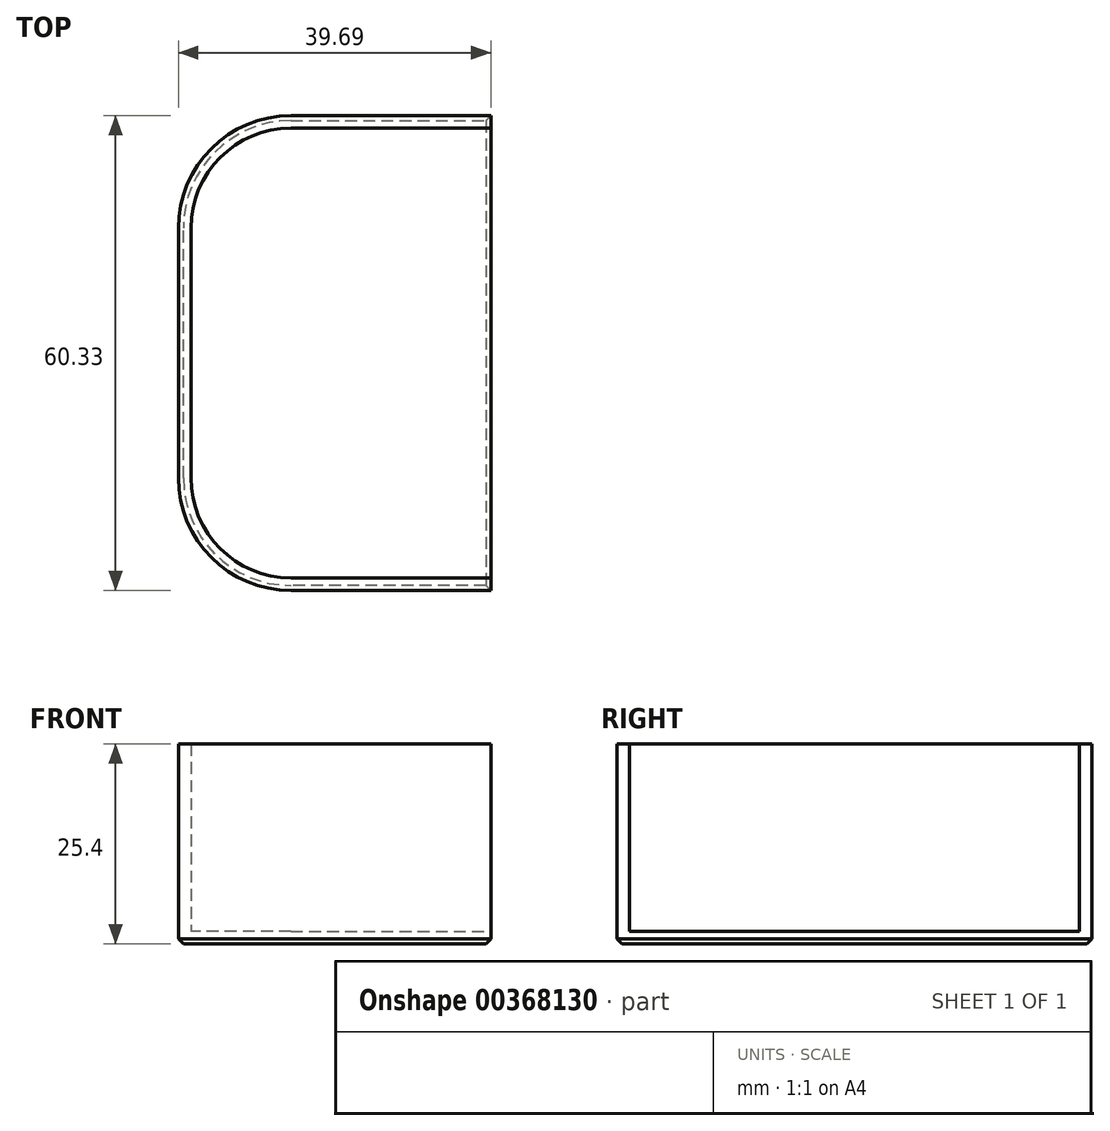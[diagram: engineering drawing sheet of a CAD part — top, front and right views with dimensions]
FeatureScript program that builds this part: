
annotation { "Feature Type Name" : "Feature", "Feature Type Description" : "" }
export const myFeature = defineFeature(function(context is Context, id is Id, definition is map)
    precondition{}
    {
        {
            var Q0;
            Q0=qCreatedBy(makeId("Top.planeOp"),FACE);
            var sketch = newSketch(context, id + "F0", { "sketchPlane" : qUnion([Q0])});
            skLineSegment(sketch, "E0.bottom", {"start": v(12.7, 0) * mm, "end": v(38.1, 0) * mm});
            skLineSegment(sketch, "E0.top", {"start": v(12.7, 57.15) * mm, "end": v(38.1, 57.15) * mm});
            skLineSegment(sketch, "E0.left", {"start": v(0, 12.7) * mm, "end": v(0, 44.45) * mm});
            skPoint(sketch, "E1.visualSharp", {"position": v(0, 57.15) * mm});
            skArc(sketch, "E1.filletArc", {"start": v(12.7, 57.15) * mm, "mid": v(3.72, 53.43) * mm, "end": v(0, 44.45) * mm});
            skPoint(sketch, "E2.visualSharp", {"position": v(0, 0) * mm});
            skArc(sketch, "E2.filletArc", {"start": v(0, 12.7) * mm, "mid": v(3.72, 3.72) * mm, "end": v(12.7, 0) * mm});
            skLineSegment(sketch, "E3", {"start": v(38.1, 57.15) * mm, "end": v(38.1, 58.74) * mm});
            skLineSegment(sketch, "E4", {"start": v(38.1, 58.74) * mm, "end": v(12.7, 58.74) * mm});
            skLineSegment(sketch, "E5", {"start": v(38.1, 0) * mm, "end": v(38.1, -1.59) * mm});
            skLineSegment(sketch, "E6", {"start": v(38.1, -1.59) * mm, "end": v(12.7, -1.59) * mm});
            skLineSegment(sketch, "E7", {"start": v(-1.59, 44.45) * mm, "end": v(-1.59, 12.7) * mm});
            skArc(sketch, "E8", {"start": v(12.7, 58.74) * mm, "mid": v(2.6, 54.55) * mm, "end": v(-1.59, 44.45) * mm});
            skArc(sketch, "E9", {"start": v(-1.59, 12.7) * mm, "mid": v(2.6, 2.6) * mm, "end": v(12.7, -1.59) * mm});
            skSolve(sketch);
        }
        {
            var Q0;
            Q0 = qSketchRegion(id + "F0", true);
            extrude(context, id + "F1", {"entities" : qUnion([Q0]), "depth" : 25.4 * mm});
        }
        {
            var Q0;
            Q0=makeQuery(id+"F1.opExtrude","CAP_FACE",FACE,{"disambiguationData":[OSD([sQuery(id+"F0.wireOp",EDGE,"E0.bottom"),sQuery(id+"F0.wireOp",EDGE,"E0.top"),sQuery(id+"F0.wireOp",EDGE,"E0.left"),sQuery(id+"F0.wireOp",EDGE,"E1.filletArc"),sQuery(id+"F0.wireOp",EDGE,"E2.filletArc"),sQuery(id+"F0.wireOp",EDGE,"E3"),sQuery(id+"F0.wireOp",EDGE,"E4"),sQuery(id+"F0.wireOp",EDGE,"E5"),sQuery(id+"F0.wireOp",EDGE,"E6"),sQuery(id+"F0.wireOp",EDGE,"E7"),sQuery(id+"F0.wireOp",EDGE,"E8"),sQuery(id+"F0.wireOp",EDGE,"E9")])],"isStart":true});
            var sketch = newSketch(context, id + "F2", { "sketchPlane" : qUnion([Q0])});
            skLineSegment(sketch, "E10.0", {"start": v(12.7, 0) * mm, "end": v(38.1, 0) * mm});
            skArc(sketch, "E10.1", {"start": v(0, -12.7) * mm, "mid": v(3.72, -3.72) * mm, "end": v(12.7, 0) * mm});
            skLineSegment(sketch, "E10.2", {"start": v(0, -12.7) * mm, "end": v(0, -44.45) * mm});
            skArc(sketch, "E10.3", {"start": v(12.7, -57.15) * mm, "mid": v(3.72, -53.43) * mm, "end": v(0, -44.45) * mm});
            skLineSegment(sketch, "E10.4", {"start": v(12.7, -57.15) * mm, "end": v(38.1, -57.15) * mm});
            skLineSegment(sketch, "E11", {"start": v(38.1, 0) * mm, "end": v(38.1, -57.15) * mm});
            skSolve(sketch);
        }
        {
            var Q0;
            Q0 = qSketchRegion(id + "F2", true);
            extrude(context, id + "F3", {"entities" : qUnion([Q0]), "operationType" : NewBodyOperationType.ADD, "oppositeDirection" : true, "depth" : 1.59 * mm});
        }
        {
            var Q0;
            Q0=makeQuery(id+"F3.boolean.opBoolean","MERGE",FACE,{"derivedFrom":[makeQuery(id+"F1.opExtrude","CAP_FACE",FACE,{"disambiguationData":[OSD([sQuery(id+"F0.wireOp",EDGE,"E0.bottom"),sQuery(id+"F0.wireOp",EDGE,"E0.top"),sQuery(id+"F0.wireOp",EDGE,"E0.left"),sQuery(id+"F0.wireOp",EDGE,"E1.filletArc"),sQuery(id+"F0.wireOp",EDGE,"E2.filletArc"),sQuery(id+"F0.wireOp",EDGE,"E3"),sQuery(id+"F0.wireOp",EDGE,"E4"),sQuery(id+"F0.wireOp",EDGE,"E5"),sQuery(id+"F0.wireOp",EDGE,"E6"),sQuery(id+"F0.wireOp",EDGE,"E7"),sQuery(id+"F0.wireOp",EDGE,"E8"),sQuery(id+"F0.wireOp",EDGE,"E9")])],"isStart":true}),makeQuery(id+"F3.opExtrude","CAP_FACE",FACE,{"disambiguationData":[OSD([sQuery(id+"F2.wireOp",EDGE,"E10.0"),sQuery(id+"F2.wireOp",EDGE,"E10.1"),sQuery(id+"F2.wireOp",EDGE,"E10.2"),sQuery(id+"F2.wireOp",EDGE,"E10.3"),sQuery(id+"F2.wireOp",EDGE,"E10.4"),sQuery(id+"F2.wireOp",EDGE,"E11")])],"isStart":true})]});
            chamfer(context, id + "F4", {"entities" : qUnion([Q0]), "width" : 0.64 * mm, "tangentPropagation" : true});
        }
    });
